# Revit family: BLAUBERG-CIVIC_EC_DB_1000
name_source: partatom
category: Mechanical Equipment
units: mm (PartAtom-declared; Revit-internal decimal feet)

## family parameters
Always vertical = Yes
Classification = None
Cut with Voids When Loaded = No
OmniClass Number = 23.75.35.14
OmniClass Title = Air Handling Units
Part Type = Normal
Room Calculation Point = No
Round Connector Dimension = Use Diameter
Shared = No
Work Plane-Based = No

## types (3) — shared parameters
Casing Material = Painted Steel White
D1 = 312 mm  [stored 1.02362 ft]
Description = Single-room ventilation unit
Drain Connection Diameter = 8 mm  [stored 0.0262467 ft]
Duct Connection Diameter = 315 mm  [stored 1.03346 ft]
Extract Air Filter = G4x2
Family Version = 1.0
Grid Material = Grid Cross
H = 542 mm  [stored 1.77822 ft]
H1 = 559 mm  [stored 1.83399 ft]
H2 = 219 mm  [stored 0.718504 ft]
Hb = 229 mm
Hc = 125 mm  [stored 0.410105 ft]
Heat Exchanger Type = counter-flow
Heat recovery efficiency (%) = 83..93
Ht = 188 mm  [stored 0.616798 ft]
L = 1202 mm  [stored 3.94357 ft]
L1 = 1242 mm  [stored 4.0748 ft]
Load Classification = HVAC
Maintenance Zone Height = 600 mm
Maintenance Zone Material = Maintenance Zone
Manufacturer = Blauberg
Maximum Air Flow = 1000 m³/h
Maximum Unit Current Without Electric Heater = 2 A
Maximum Unit Power Without Electric Heater = 260 W
Number of Poles = 3
Power Factor = 1
RPM (min-1) = 2070
SEC Class = A+
Sound Pressure Level at 1 m (dBA) = 35
Sound Pressure Level at 3 m (dBA) = 25
Supply Air Filter = G4x2 + (option: F7 x 2)
Transported Air Temperature (°C) = –25 …+40
URL = https://blaubergventilatoren.de
Voltage = 400 V
W = 2327 mm  [stored 7.63451 ft]
W1 = 194 mm  [stored 0.636483 ft]
W2 = 1764 mm  [stored 5.7874 ft]
WLeftPart = 603 mm
WRightPart = 423 mm  [stored 1.3878 ft]
dL = 5 mm  [stored 0.0164042 ft]
dW = 5 mm  [stored 0.0164042 ft]
ofH = 120 mm  [stored 0.393701 ft]
ofLeft = 628 mm  [stored 2.06037 ft]
ofLeftCenter = 828 mm  [stored 2.71654 ft]
ofRight = 470 mm  [stored 1.54199 ft]
ofRightCenter = 670 mm  [stored 2.19816 ft]
ofW = 400 mm  [stored 1.31234 ft]
osBack = 408 mm
osH = 168 mm  [stored 0.551181 ft]
osW = 658 mm  [stored 2.15879 ft]

## per-type parameters (varying)
| type | Current | Maximum Unit Current With Electric Heater | Power | Preheater power | Reheater power | Type Comments | Weight |
| CIVIC EC DB 1000 S21 | 2 A | 2 A | 260 W | 0 W | 0 W | Single-room ventilation unit  CIVIC EC DB 1000 S21 | 267.00 kg |
| CIVIC EC DBE 1000 S21 | 11 A | 11 A | 6560 W | 6300 W | 0 W | Single-room ventilation unit  CIVIC EC DBE 1000 S21 | 271.00 kg |
| CIVIC EC DBE2 1000 S21 | 21 A | 21 A | 12860 W | 6300 W | 6300 W | Single-room ventilation unit  CIVIC EC DBE2 1000 S21 | 275.00 kg |

note: column(s) folded — value = type name in every type: Model

note: [stored X ft] marks values corroborated as IEEE doubles in the binary element streams (Revit-internal decimal feet)

## geometry (parser evidence)
native form markers: Sweep x6
no freeform markers — native parametric forms only
